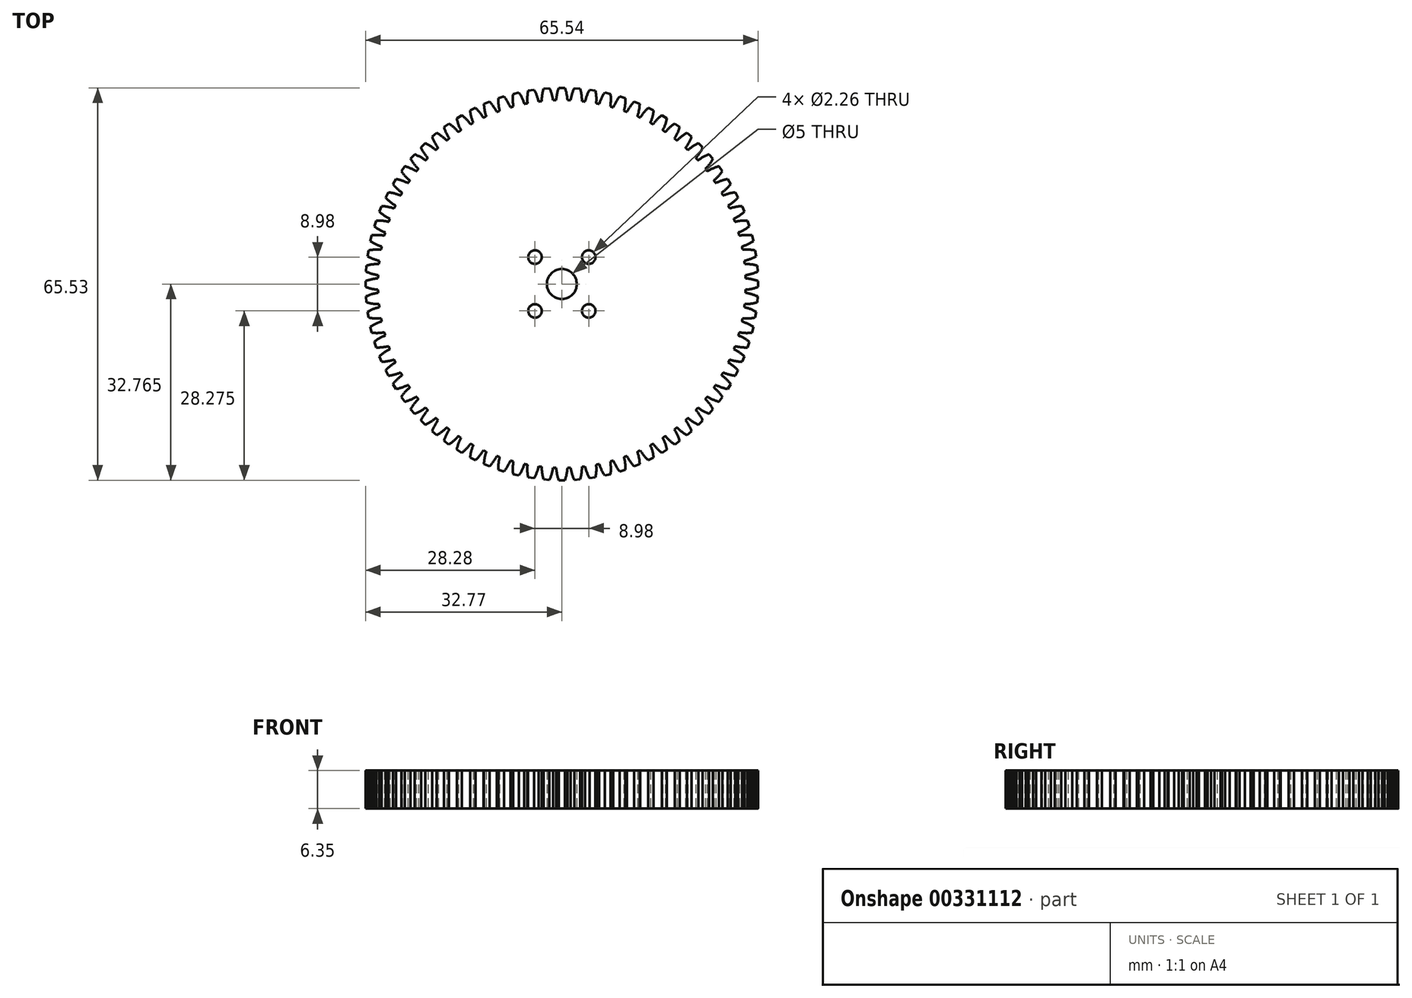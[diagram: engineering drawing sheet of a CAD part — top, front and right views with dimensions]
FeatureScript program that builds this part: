
annotation { "Feature Type Name" : "Feature", "Feature Type Description" : "" }
export const myFeature = defineFeature(function(context is Context, id is Id, definition is map)
    precondition{}
    {
        {
            var Q0;
            Q0=qCreatedBy(makeId("Top.planeOp"),FACE);
            var sketch = newSketch(context, id + "F0", { "sketchPlane" : qUnion([Q0])});
            skLineSegment(sketch, "E0", {"start": v(-0.5, 21.15) * mm, "end": v(0.5, 21.15) * mm});
            skArc(sketch, "E1", {"start": v(-0.5, 21.15) * mm, "mid": v(-0.8, 20.14) * mm, "end": v(-0.94, 19.09) * mm});
            skArc(sketch, "E2.MirrorCS", {"start": v(0.5, 21.15) * mm, "mid": v(0.8, 20.14) * mm, "end": v(0.94, 19.09) * mm});
            skPoint(sketch, "E3.center", {"position": v(0, -11.62) * mm});
            skPoint(sketch, "E4.center", {"position": v(0, 0) * mm});
            skCircle(sketch, "E5.1.1", {"center": v(-4.5, -7.13) * mm, "radius": 1.13 * mm});
            skCircle(sketch, "E5.3.1", {"center": v(-4.5, -16.1) * mm, "radius": 1.13 * mm});
            skCircle(sketch, "E5.5.1", {"center": v(4.5, -16.1) * mm, "radius": 1.13 * mm});
            skCircle(sketch, "E5.7.1", {"center": v(4.5, -7.13) * mm, "radius": 1.13 * mm});
            skArc(sketch, "E6", {"start": v(3.31, 18.92) * mm, "mid": v(2.13, 19.03) * mm, "end": v(0.94, 19.09) * mm});
            skArc(sketch, "E7.1.0", {"start": v(-2.07, 21.09) * mm, "mid": v(-1.7, 20.1) * mm, "end": v(-1.48, 19.07) * mm});
            skLineSegment(sketch, "E7.1.1", {"start": v(-3.07, 21.01) * mm, "end": v(-2.07, 21.09) * mm});
            skArc(sketch, "E7.1.2", {"start": v(-3.07, 21.01) * mm, "mid": v(-3.28, 19.97) * mm, "end": v(-3.34, 18.92) * mm});
            skArc(sketch, "E7.1.3", {"start": v(0.9, 19.09) * mm, "mid": v(-0.28, 19.1) * mm, "end": v(-1.48, 19.07) * mm});
            skArc(sketch, "E7.2.0", {"start": v(-4.63, 20.83) * mm, "mid": v(-4.18, 19.87) * mm, "end": v(-3.88, 18.86) * mm});
            skLineSegment(sketch, "E7.2.1", {"start": v(-5.62, 20.67) * mm, "end": v(-4.63, 20.83) * mm});
            skArc(sketch, "E7.2.2", {"start": v(-5.62, 20.67) * mm, "mid": v(-5.75, 19.62) * mm, "end": v(-5.73, 18.56) * mm});
            skArc(sketch, "E7.2.3", {"start": v(-1.5, 19.06) * mm, "mid": v(-2.7, 18.98) * mm, "end": v(-3.88, 18.86) * mm});
            skArc(sketch, "E7.3.0", {"start": v(-7.16, 20.36) * mm, "mid": v(-6.64, 19.44) * mm, "end": v(-6.26, 18.46) * mm});
            skLineSegment(sketch, "E7.3.1", {"start": v(-8.14, 20.13) * mm, "end": v(-7.16, 20.36) * mm});
            skArc(sketch, "E7.3.2", {"start": v(-8.14, 20.13) * mm, "mid": v(-8.18, 19.07) * mm, "end": v(-8.08, 18.02) * mm});
            skArc(sketch, "E7.3.3", {"start": v(-3.9, 18.85) * mm, "mid": v(-5.09, 18.68) * mm, "end": v(-6.26, 18.46) * mm});
            skArc(sketch, "E7.4.0", {"start": v(-9.65, 19.7) * mm, "mid": v(-9.06, 18.83) * mm, "end": v(-8.6, 17.87) * mm});
            skLineSegment(sketch, "E7.4.1", {"start": v(-10.6, 19.4) * mm, "end": v(-9.65, 19.7) * mm});
            skArc(sketch, "E7.4.2", {"start": v(-10.6, 19.4) * mm, "mid": v(-10.57, 18.34) * mm, "end": v(-10.38, 17.3) * mm});
            skArc(sketch, "E7.4.3", {"start": v(-6.29, 18.45) * mm, "mid": v(-7.45, 18.18) * mm, "end": v(-8.6, 17.87) * mm});
            skArc(sketch, "E7.5.0", {"start": v(-12.08, 18.85) * mm, "mid": v(-11.42, 18.02) * mm, "end": v(-10.88, 17.1) * mm});
            skLineSegment(sketch, "E7.5.1", {"start": v(-13, 18.47) * mm, "end": v(-12.08, 18.85) * mm});
            skArc(sketch, "E7.5.2", {"start": v(-13, 18.47) * mm, "mid": v(-12.88, 17.41) * mm, "end": v(-12.61, 16.4) * mm});
            skArc(sketch, "E7.5.3", {"start": v(-8.63, 17.87) * mm, "mid": v(-9.76, 17.5) * mm, "end": v(-10.88, 17.1) * mm});
            skArc(sketch, "E7.6.0", {"start": v(-14.43, 17.8) * mm, "mid": v(-13.7, 17.04) * mm, "end": v(-13.1, 16.17) * mm});
            skLineSegment(sketch, "E7.6.1", {"start": v(-15.32, 17.35) * mm, "end": v(-14.43, 17.8) * mm});
            skArc(sketch, "E7.6.2", {"start": v(-15.32, 17.35) * mm, "mid": v(-15.12, 16.31) * mm, "end": v(-14.77, 15.32) * mm});
            skArc(sketch, "E7.6.3", {"start": v(-10.91, 17.1) * mm, "mid": v(-12.02, 16.65) * mm, "end": v(-13.1, 16.17) * mm});
            skArc(sketch, "E7.7.0", {"start": v(-16.7, 16.58) * mm, "mid": v(-15.91, 15.87) * mm, "end": v(-15.24, 15.05) * mm});
            skLineSegment(sketch, "E7.7.1", {"start": v(-17.55, 16.06) * mm, "end": v(-16.7, 16.58) * mm});
            skArc(sketch, "E7.7.2", {"start": v(-17.55, 16.06) * mm, "mid": v(-17.27, 15.04) * mm, "end": v(-16.84, 14.07) * mm});
            skArc(sketch, "E7.7.3", {"start": v(-13.13, 16.15) * mm, "mid": v(-14.2, 15.62) * mm, "end": v(-15.24, 15.05) * mm});
            skArc(sketch, "E7.8.0", {"start": v(-18.85, 15.19) * mm, "mid": v(-18.02, 14.54) * mm, "end": v(-17.29, 13.77) * mm});
            skLineSegment(sketch, "E7.8.1", {"start": v(-19.66, 14.6) * mm, "end": v(-18.85, 15.19) * mm});
            skArc(sketch, "E7.8.2", {"start": v(-19.66, 14.6) * mm, "mid": v(-19.3, 13.6) * mm, "end": v(-18.8, 12.67) * mm});
            skArc(sketch, "E7.8.3", {"start": v(-15.27, 15.04) * mm, "mid": v(-16.3, 14.43) * mm, "end": v(-17.29, 13.77) * mm});
            skArc(sketch, "E7.9.0", {"start": v(-20.9, 13.63) * mm, "mid": v(-20.02, 13.04) * mm, "end": v(-19.23, 12.34) * mm});
            skLineSegment(sketch, "E7.9.1", {"start": v(-21.66, 12.98) * mm, "end": v(-20.9, 13.63) * mm});
            skArc(sketch, "E7.9.2", {"start": v(-21.66, 12.98) * mm, "mid": v(-21.22, 12.01) * mm, "end": v(-20.65, 11.12) * mm});
            skArc(sketch, "E7.9.3", {"start": v(-17.31, 13.76) * mm, "mid": v(-18.28, 13.07) * mm, "end": v(-19.23, 12.34) * mm});
            skArc(sketch, "E7.10.0", {"start": v(-22.82, 11.9) * mm, "mid": v(-21.89, 11.4) * mm, "end": v(-21.05, 10.76) * mm});
            skLineSegment(sketch, "E7.10.1", {"start": v(-23.52, 11.2) * mm, "end": v(-22.82, 11.9) * mm});
            skArc(sketch, "E7.10.2", {"start": v(-23.52, 11.2) * mm, "mid": v(-23.01, 10.27) * mm, "end": v(-22.37, 9.43) * mm});
            skArc(sketch, "E7.10.3", {"start": v(-19.25, 12.32) * mm, "mid": v(-20.16, 11.56) * mm, "end": v(-21.05, 10.76) * mm});
            skArc(sketch, "E7.11.0", {"start": v(-24.6, 10.04) * mm, "mid": v(-23.63, 9.6) * mm, "end": v(-22.74, 9.04) * mm});
            skLineSegment(sketch, "E7.11.1", {"start": v(-25.24, 9.28) * mm, "end": v(-24.6, 10.04) * mm});
            skArc(sketch, "E7.11.2", {"start": v(-25.24, 9.28) * mm, "mid": v(-24.66, 8.4) * mm, "end": v(-23.95, 7.61) * mm});
            skArc(sketch, "E7.11.3", {"start": v(-21.07, 10.74) * mm, "mid": v(-21.92, 9.9) * mm, "end": v(-22.74, 9.04) * mm});
            skArc(sketch, "E7.12.0", {"start": v(-26.21, 8.05) * mm, "mid": v(-25.22, 7.7) * mm, "end": v(-24.29, 7.19) * mm});
            skLineSegment(sketch, "E7.12.1", {"start": v(-26.8, 7.24) * mm, "end": v(-26.21, 8.05) * mm});
            skArc(sketch, "E7.12.2", {"start": v(-26.8, 7.24) * mm, "mid": v(-26.15, 6.4) * mm, "end": v(-25.39, 5.67) * mm});
            skArc(sketch, "E7.12.3", {"start": v(-22.76, 9.01) * mm, "mid": v(-23.54, 8.12) * mm, "end": v(-24.29, 7.19) * mm});
            skArc(sketch, "E7.13.0", {"start": v(-27.68, 5.93) * mm, "mid": v(-26.66, 5.65) * mm, "end": v(-25.69, 5.23) * mm});
            skLineSegment(sketch, "E7.13.1", {"start": v(-28.2, 5.08) * mm, "end": v(-27.68, 5.93) * mm});
            skArc(sketch, "E7.13.2", {"start": v(-28.2, 5.08) * mm, "mid": v(-27.49, 4.3) * mm, "end": v(-26.67, 3.63) * mm});
            skArc(sketch, "E7.13.3", {"start": v(-24.3, 7.16) * mm, "mid": v(-25.02, 6.2) * mm, "end": v(-25.69, 5.23) * mm});
            skArc(sketch, "E7.14.0", {"start": v(-28.97, 3.7) * mm, "mid": v(-27.93, 3.5) * mm, "end": v(-26.93, 3.16) * mm});
            skLineSegment(sketch, "E7.14.1", {"start": v(-29.42, 2.81) * mm, "end": v(-28.97, 3.7) * mm});
            skArc(sketch, "E7.14.2", {"start": v(-29.42, 2.81) * mm, "mid": v(-28.65, 2.1) * mm, "end": v(-27.78, 1.49) * mm});
            skArc(sketch, "E7.14.3", {"start": v(-25.7, 5.2) * mm, "mid": v(-26.34, 4.2) * mm, "end": v(-26.93, 3.16) * mm});
            skArc(sketch, "E7.15.0", {"start": v(-30.08, 1.39) * mm, "mid": v(-29.03, 1.27) * mm, "end": v(-28, 1) * mm});
            skLineSegment(sketch, "E7.15.1", {"start": v(-30.46, 0.46) * mm, "end": v(-30.08, 1.39) * mm});
            skArc(sketch, "E7.15.2", {"start": v(-30.46, 0.46) * mm, "mid": v(-29.64, -0.2) * mm, "end": v(-28.72, -0.73) * mm});
            skArc(sketch, "E7.15.3", {"start": v(-26.95, 3.13) * mm, "mid": v(-27.5, 2.08) * mm, "end": v(-28, 1) * mm});
            skArc(sketch, "E7.16.0", {"start": v(-31, -1.01) * mm, "mid": v(-29.95, -1.05) * mm, "end": v(-28.91, -1.24) * mm});
            skLineSegment(sketch, "E7.16.1", {"start": v(-31.32, -1.97) * mm, "end": v(-31, -1.01) * mm});
            skArc(sketch, "E7.16.2", {"start": v(-31.32, -1.97) * mm, "mid": v(-30.44, -2.56) * mm, "end": v(-29.49, -3.02) * mm});
            skArc(sketch, "E7.16.3", {"start": v(-28.02, 0.97) * mm, "mid": v(-28.49, -0.12) * mm, "end": v(-28.91, -1.24) * mm});
            skArc(sketch, "E7.17.0", {"start": v(-31.74, -3.48) * mm, "mid": v(-30.69, -3.43) * mm, "end": v(-29.64, -3.54) * mm});
            skLineSegment(sketch, "E7.17.1", {"start": v(-31.98, -4.45) * mm, "end": v(-31.74, -3.48) * mm});
            skArc(sketch, "E7.17.2", {"start": v(-31.98, -4.45) * mm, "mid": v(-31.06, -4.98) * mm, "end": v(-30.07, -5.36) * mm});
            skArc(sketch, "E7.17.3", {"start": v(-28.92, -1.27) * mm, "mid": v(-29.3, -2.4) * mm, "end": v(-29.64, -3.54) * mm});
            skArc(sketch, "E7.18.0", {"start": v(-32.28, -6) * mm, "mid": v(-31.24, -5.86) * mm, "end": v(-30.18, -5.89) * mm});
            skLineSegment(sketch, "E7.18.1", {"start": v(-32.44, -6.98) * mm, "end": v(-32.28, -6) * mm});
            skArc(sketch, "E7.18.2", {"start": v(-32.44, -6.98) * mm, "mid": v(-31.48, -7.43) * mm, "end": v(-30.47, -7.74) * mm});
            skArc(sketch, "E7.18.3", {"start": v(-29.64, -3.57) * mm, "mid": v(-29.93, -4.72) * mm, "end": v(-30.18, -5.89) * mm});
            skArc(sketch, "E7.19.0", {"start": v(-32.63, -8.55) * mm, "mid": v(-31.6, -8.33) * mm, "end": v(-30.53, -8.27) * mm});
            skLineSegment(sketch, "E7.19.1", {"start": v(-32.7, -9.54) * mm, "end": v(-32.63, -8.55) * mm});
            skArc(sketch, "E7.19.2", {"start": v(-32.7, -9.54) * mm, "mid": v(-31.71, -9.92) * mm, "end": v(-30.68, -10.14) * mm});
            skArc(sketch, "E7.19.3", {"start": v(-30.18, -5.92) * mm, "mid": v(-30.38, -7.1) * mm, "end": v(-30.53, -8.27) * mm});
            skArc(sketch, "E7.20.0", {"start": v(-32.77, -11.12) * mm, "mid": v(-31.75, -10.82) * mm, "end": v(-30.7, -10.68) * mm});
            skLineSegment(sketch, "E7.20.1", {"start": v(-32.77, -12.12) * mm, "end": v(-32.77, -11.12) * mm});
            skArc(sketch, "E7.20.2", {"start": v(-32.77, -12.12) * mm, "mid": v(-31.75, -12.4) * mm, "end": v(-30.7, -12.55) * mm});
            skArc(sketch, "E7.20.3", {"start": v(-30.54, -8.3) * mm, "mid": v(-30.64, -9.49) * mm, "end": v(-30.7, -10.68) * mm});
            skArc(sketch, "E7.21.0", {"start": v(-32.7, -13.69) * mm, "mid": v(-31.71, -13.31) * mm, "end": v(-30.68, -13.1) * mm});
            skLineSegment(sketch, "E7.21.1", {"start": v(-32.63, -14.68) * mm, "end": v(-32.7, -13.69) * mm});
            skArc(sketch, "E7.21.2", {"start": v(-32.63, -14.68) * mm, "mid": v(-31.6, -14.9) * mm, "end": v(-30.53, -14.96) * mm});
            skArc(sketch, "E7.21.3", {"start": v(-30.7, -10.7) * mm, "mid": v(-30.72, -11.9) * mm, "end": v(-30.68, -13.1) * mm});
            skArc(sketch, "E7.22.0", {"start": v(-32.44, -16.25) * mm, "mid": v(-31.48, -15.8) * mm, "end": v(-30.47, -15.5) * mm});
            skLineSegment(sketch, "E7.22.1", {"start": v(-32.28, -17.23) * mm, "end": v(-32.44, -16.25) * mm});
            skArc(sketch, "E7.22.2", {"start": v(-32.28, -17.23) * mm, "mid": v(-31.24, -17.37) * mm, "end": v(-30.18, -17.34) * mm});
            skArc(sketch, "E7.22.3", {"start": v(-30.68, -13.12) * mm, "mid": v(-30.6, -14.3) * mm, "end": v(-30.47, -15.5) * mm});
            skArc(sketch, "E7.23.0", {"start": v(-31.98, -18.78) * mm, "mid": v(-31.06, -18.25) * mm, "end": v(-30.07, -17.87) * mm});
            skLineSegment(sketch, "E7.23.1", {"start": v(-31.74, -19.75) * mm, "end": v(-31.98, -18.78) * mm});
            skArc(sketch, "E7.23.2", {"start": v(-31.74, -19.75) * mm, "mid": v(-30.69, -19.8) * mm, "end": v(-29.64, -19.7) * mm});
            skArc(sketch, "E7.23.3", {"start": v(-30.47, -15.52) * mm, "mid": v(-30.3, -16.7) * mm, "end": v(-30.07, -17.87) * mm});
            skArc(sketch, "E7.24.0", {"start": v(-31.32, -21.26) * mm, "mid": v(-30.44, -20.67) * mm, "end": v(-29.49, -20.21) * mm});
            skLineSegment(sketch, "E7.24.1", {"start": v(-31, -22.22) * mm, "end": v(-31.32, -21.26) * mm});
            skArc(sketch, "E7.24.2", {"start": v(-31, -22.22) * mm, "mid": v(-29.95, -22.18) * mm, "end": v(-28.91, -22) * mm});
            skArc(sketch, "E7.24.3", {"start": v(-30.07, -17.9) * mm, "mid": v(-29.8, -19.06) * mm, "end": v(-29.49, -20.21) * mm});
            skArc(sketch, "E7.25.0", {"start": v(-30.46, -23.7) * mm, "mid": v(-29.64, -23.03) * mm, "end": v(-28.72, -22.5) * mm});
            skLineSegment(sketch, "E7.25.1", {"start": v(-30.08, -24.62) * mm, "end": v(-30.46, -23.7) * mm});
            skArc(sketch, "E7.25.2", {"start": v(-30.08, -24.62) * mm, "mid": v(-29.03, -24.5) * mm, "end": v(-28, -24.23) * mm});
            skArc(sketch, "E7.25.3", {"start": v(-29.48, -20.24) * mm, "mid": v(-29.12, -21.38) * mm, "end": v(-28.72, -22.5) * mm});
            skArc(sketch, "E7.26.0", {"start": v(-29.42, -26.05) * mm, "mid": v(-28.65, -25.32) * mm, "end": v(-27.78, -24.72) * mm});
            skLineSegment(sketch, "E7.26.1", {"start": v(-28.97, -26.94) * mm, "end": v(-29.42, -26.05) * mm});
            skArc(sketch, "E7.26.2", {"start": v(-28.97, -26.94) * mm, "mid": v(-27.93, -26.74) * mm, "end": v(-26.93, -26.39) * mm});
            skArc(sketch, "E7.26.3", {"start": v(-28.71, -22.53) * mm, "mid": v(-28.27, -23.63) * mm, "end": v(-27.78, -24.72) * mm});
            skArc(sketch, "E7.27.0", {"start": v(-28.2, -28.3) * mm, "mid": v(-27.49, -27.53) * mm, "end": v(-26.67, -26.86) * mm});
            skLineSegment(sketch, "E7.27.1", {"start": v(-27.68, -29.16) * mm, "end": v(-28.2, -28.3) * mm});
            skArc(sketch, "E7.27.2", {"start": v(-27.68, -29.16) * mm, "mid": v(-26.66, -28.88) * mm, "end": v(-25.69, -28.46) * mm});
            skArc(sketch, "E7.27.3", {"start": v(-27.77, -24.75) * mm, "mid": v(-27.24, -25.81) * mm, "end": v(-26.67, -26.86) * mm});
            skArc(sketch, "E7.28.0", {"start": v(-26.8, -30.47) * mm, "mid": v(-26.15, -29.63) * mm, "end": v(-25.39, -28.9) * mm});
            skLineSegment(sketch, "E7.28.1", {"start": v(-26.21, -31.28) * mm, "end": v(-26.8, -30.47) * mm});
            skArc(sketch, "E7.28.2", {"start": v(-26.21, -31.28) * mm, "mid": v(-25.22, -30.92) * mm, "end": v(-24.29, -30.42) * mm});
            skArc(sketch, "E7.28.3", {"start": v(-26.65, -26.88) * mm, "mid": v(-26.04, -27.9) * mm, "end": v(-25.39, -28.9) * mm});
            skArc(sketch, "E7.29.0", {"start": v(-25.24, -32.51) * mm, "mid": v(-24.66, -31.63) * mm, "end": v(-23.95, -30.84) * mm});
            skLineSegment(sketch, "E7.29.1", {"start": v(-24.6, -33.28) * mm, "end": v(-25.24, -32.51) * mm});
            skArc(sketch, "E7.29.2", {"start": v(-24.6, -33.28) * mm, "mid": v(-23.63, -32.84) * mm, "end": v(-22.74, -32.27) * mm});
            skArc(sketch, "E7.29.3", {"start": v(-25.37, -28.93) * mm, "mid": v(-24.68, -29.9) * mm, "end": v(-23.95, -30.84) * mm});
            skArc(sketch, "E7.30.0", {"start": v(-23.52, -34.43) * mm, "mid": v(-23.01, -33.5) * mm, "end": v(-22.37, -32.66) * mm});
            skLineSegment(sketch, "E7.30.1", {"start": v(-22.82, -35.14) * mm, "end": v(-23.52, -34.43) * mm});
            skArc(sketch, "E7.30.2", {"start": v(-22.82, -35.14) * mm, "mid": v(-21.89, -34.63) * mm, "end": v(-21.05, -33.99) * mm});
            skArc(sketch, "E7.30.3", {"start": v(-23.94, -30.87) * mm, "mid": v(-23.17, -31.78) * mm, "end": v(-22.37, -32.66) * mm});
            skArc(sketch, "E7.31.0", {"start": v(-21.66, -36.2) * mm, "mid": v(-21.22, -35.24) * mm, "end": v(-20.65, -34.35) * mm});
            skLineSegment(sketch, "E7.31.1", {"start": v(-20.9, -36.86) * mm, "end": v(-21.66, -36.2) * mm});
            skArc(sketch, "E7.31.2", {"start": v(-20.9, -36.86) * mm, "mid": v(-20.02, -36.27) * mm, "end": v(-19.23, -35.57) * mm});
            skArc(sketch, "E7.31.3", {"start": v(-22.35, -32.68) * mm, "mid": v(-21.52, -33.54) * mm, "end": v(-20.65, -34.35) * mm});
            skArc(sketch, "E7.32.0", {"start": v(-19.66, -37.83) * mm, "mid": v(-19.3, -36.83) * mm, "end": v(-18.8, -35.9) * mm});
            skLineSegment(sketch, "E7.32.1", {"start": v(-18.85, -38.42) * mm, "end": v(-19.66, -37.83) * mm});
            skArc(sketch, "E7.32.2", {"start": v(-18.85, -38.42) * mm, "mid": v(-18.02, -37.77) * mm, "end": v(-17.29, -37) * mm});
            skArc(sketch, "E7.32.3", {"start": v(-20.63, -34.37) * mm, "mid": v(-19.73, -35.16) * mm, "end": v(-18.8, -35.9) * mm});
            skArc(sketch, "E7.33.0", {"start": v(-17.55, -39.3) * mm, "mid": v(-17.27, -38.27) * mm, "end": v(-16.84, -37.3) * mm});
            skLineSegment(sketch, "E7.33.1", {"start": v(-16.7, -39.81) * mm, "end": v(-17.55, -39.3) * mm});
            skArc(sketch, "E7.33.2", {"start": v(-16.7, -39.81) * mm, "mid": v(-15.91, -39.1) * mm, "end": v(-15.24, -38.28) * mm});
            skArc(sketch, "E7.33.3", {"start": v(-18.78, -35.92) * mm, "mid": v(-17.82, -36.63) * mm, "end": v(-16.84, -37.3) * mm});
            skArc(sketch, "E7.34.0", {"start": v(-15.32, -40.58) * mm, "mid": v(-15.12, -39.54) * mm, "end": v(-14.77, -38.55) * mm});
            skLineSegment(sketch, "E7.34.1", {"start": v(-14.43, -41.04) * mm, "end": v(-15.32, -40.58) * mm});
            skArc(sketch, "E7.34.2", {"start": v(-14.43, -41.04) * mm, "mid": v(-13.7, -40.27) * mm, "end": v(-13.1, -39.4) * mm});
            skArc(sketch, "E7.34.3", {"start": v(-16.81, -37.32) * mm, "mid": v(-15.8, -37.95) * mm, "end": v(-14.77, -38.55) * mm});
            skArc(sketch, "E7.35.0", {"start": v(-13, -41.7) * mm, "mid": v(-12.88, -40.64) * mm, "end": v(-12.61, -39.62) * mm});
            skLineSegment(sketch, "E7.35.1", {"start": v(-12.08, -42.08) * mm, "end": v(-13, -41.7) * mm});
            skArc(sketch, "E7.35.2", {"start": v(-12.08, -42.08) * mm, "mid": v(-11.42, -41.25) * mm, "end": v(-10.88, -40.34) * mm});
            skArc(sketch, "E7.35.3", {"start": v(-14.75, -38.56) * mm, "mid": v(-13.7, -39.11) * mm, "end": v(-12.61, -39.62) * mm});
            skArc(sketch, "E7.36.0", {"start": v(-10.6, -42.62) * mm, "mid": v(-10.57, -41.57) * mm, "end": v(-10.38, -40.53) * mm});
            skLineSegment(sketch, "E7.36.1", {"start": v(-9.65, -42.93) * mm, "end": v(-10.6, -42.62) * mm});
            skArc(sketch, "E7.36.2", {"start": v(-9.65, -42.93) * mm, "mid": v(-9.06, -42.06) * mm, "end": v(-8.6, -41.1) * mm});
            skArc(sketch, "E7.36.3", {"start": v(-12.59, -39.63) * mm, "mid": v(-11.5, -40.1) * mm, "end": v(-10.38, -40.53) * mm});
            skArc(sketch, "E7.37.0", {"start": v(-8.14, -43.36) * mm, "mid": v(-8.18, -42.3) * mm, "end": v(-8.08, -41.25) * mm});
            skLineSegment(sketch, "E7.37.1", {"start": v(-7.16, -43.6) * mm, "end": v(-8.14, -43.36) * mm});
            skArc(sketch, "E7.37.2", {"start": v(-7.16, -43.6) * mm, "mid": v(-6.64, -42.67) * mm, "end": v(-6.26, -41.69) * mm});
            skArc(sketch, "E7.37.3", {"start": v(-10.35, -40.54) * mm, "mid": v(-9.22, -40.92) * mm, "end": v(-8.08, -41.25) * mm});
            skArc(sketch, "E7.38.0", {"start": v(-5.62, -43.9) * mm, "mid": v(-5.75, -42.85) * mm, "end": v(-5.73, -41.8) * mm});
            skLineSegment(sketch, "E7.38.1", {"start": v(-4.63, -44.06) * mm, "end": v(-5.62, -43.9) * mm});
            skArc(sketch, "E7.38.2", {"start": v(-4.63, -44.06) * mm, "mid": v(-4.18, -43.1) * mm, "end": v(-3.88, -42.09) * mm});
            skArc(sketch, "E7.38.3", {"start": v(-8.05, -41.26) * mm, "mid": v(-6.9, -41.55) * mm, "end": v(-5.73, -41.8) * mm});
            skArc(sketch, "E7.39.0", {"start": v(-3.07, -44.24) * mm, "mid": v(-3.28, -43.2) * mm, "end": v(-3.34, -42.15) * mm});
            skLineSegment(sketch, "E7.39.1", {"start": v(-2.07, -44.32) * mm, "end": v(-3.07, -44.24) * mm});
            skArc(sketch, "E7.39.2", {"start": v(-2.07, -44.32) * mm, "mid": v(-1.7, -43.33) * mm, "end": v(-1.48, -42.3) * mm});
            skArc(sketch, "E7.39.3", {"start": v(-5.7, -41.8) * mm, "mid": v(-4.52, -42) * mm, "end": v(-3.34, -42.15) * mm});
            skCircle(sketch, "E8", {"center": v(0, -11.62) * mm, "radius": 2.5 * mm});
            skLineSegment(sketch, "E9.4.40.0", {"start": v(0.5, -44.38) * mm, "end": v(-0.5, -44.38) * mm});
            skArc(sketch, "E9.7.40.0", {"start": v(0.5, -44.38) * mm, "mid": v(0.8, -43.37) * mm, "end": v(0.94, -42.32) * mm});
            skArc(sketch, "E9.11.40.0", {"start": v(-3.31, -42.15) * mm, "mid": v(-2.13, -42.26) * mm, "end": v(-0.94, -42.32) * mm});
            skArc(sketch, "E9.12.40.0", {"start": v(-0.5, -44.38) * mm, "mid": v(-0.8, -43.37) * mm, "end": v(-0.94, -42.32) * mm});
            skLineSegment(sketch, "E9.4.41.0", {"start": v(3.07, -44.24) * mm, "end": v(2.07, -44.32) * mm});
            skArc(sketch, "E9.7.41.0", {"start": v(3.07, -44.24) * mm, "mid": v(3.28, -43.2) * mm, "end": v(3.34, -42.15) * mm});
            skArc(sketch, "E9.11.41.0", {"start": v(-0.9, -42.32) * mm, "mid": v(0.28, -42.33) * mm, "end": v(1.48, -42.3) * mm});
            skArc(sketch, "E9.12.41.0", {"start": v(2.07, -44.32) * mm, "mid": v(1.7, -43.33) * mm, "end": v(1.48, -42.3) * mm});
            skLineSegment(sketch, "E9.4.42.0", {"start": v(5.62, -43.9) * mm, "end": v(4.63, -44.06) * mm});
            skArc(sketch, "E9.7.42.0", {"start": v(5.62, -43.9) * mm, "mid": v(5.75, -42.85) * mm, "end": v(5.73, -41.8) * mm});
            skArc(sketch, "E9.11.42.0", {"start": v(1.5, -42.3) * mm, "mid": v(2.7, -42.21) * mm, "end": v(3.88, -42.09) * mm});
            skArc(sketch, "E9.12.42.0", {"start": v(4.63, -44.06) * mm, "mid": v(4.18, -43.1) * mm, "end": v(3.88, -42.09) * mm});
            skLineSegment(sketch, "E9.4.43.0", {"start": v(8.14, -43.36) * mm, "end": v(7.16, -43.6) * mm});
            skArc(sketch, "E9.7.43.0", {"start": v(8.14, -43.36) * mm, "mid": v(8.18, -42.3) * mm, "end": v(8.08, -41.25) * mm});
            skArc(sketch, "E9.11.43.0", {"start": v(3.9, -42.08) * mm, "mid": v(5.09, -41.9) * mm, "end": v(6.26, -41.69) * mm});
            skArc(sketch, "E9.12.43.0", {"start": v(7.16, -43.6) * mm, "mid": v(6.64, -42.67) * mm, "end": v(6.26, -41.69) * mm});
            skLineSegment(sketch, "E9.4.44.0", {"start": v(10.6, -42.62) * mm, "end": v(9.65, -42.93) * mm});
            skArc(sketch, "E9.7.44.0", {"start": v(10.6, -42.62) * mm, "mid": v(10.57, -41.57) * mm, "end": v(10.38, -40.53) * mm});
            skArc(sketch, "E9.11.44.0", {"start": v(6.29, -41.68) * mm, "mid": v(7.45, -41.42) * mm, "end": v(8.6, -41.1) * mm});
            skArc(sketch, "E9.12.44.0", {"start": v(9.65, -42.93) * mm, "mid": v(9.06, -42.06) * mm, "end": v(8.6, -41.1) * mm});
            skLineSegment(sketch, "E9.4.45.0", {"start": v(13, -41.7) * mm, "end": v(12.08, -42.08) * mm});
            skArc(sketch, "E9.7.45.0", {"start": v(13, -41.7) * mm, "mid": v(12.88, -40.64) * mm, "end": v(12.61, -39.62) * mm});
            skArc(sketch, "E9.11.45.0", {"start": v(8.63, -41.1) * mm, "mid": v(9.76, -40.74) * mm, "end": v(10.88, -40.34) * mm});
            skArc(sketch, "E9.12.45.0", {"start": v(12.08, -42.08) * mm, "mid": v(11.42, -41.25) * mm, "end": v(10.88, -40.34) * mm});
            skLineSegment(sketch, "E9.4.46.0", {"start": v(15.32, -40.58) * mm, "end": v(14.43, -41.04) * mm});
            skArc(sketch, "E9.7.46.0", {"start": v(15.32, -40.58) * mm, "mid": v(15.12, -39.54) * mm, "end": v(14.77, -38.55) * mm});
            skArc(sketch, "E9.11.46.0", {"start": v(10.91, -40.33) * mm, "mid": v(12.02, -39.88) * mm, "end": v(13.1, -39.4) * mm});
            skArc(sketch, "E9.12.46.0", {"start": v(14.43, -41.04) * mm, "mid": v(13.7, -40.27) * mm, "end": v(13.1, -39.4) * mm});
            skLineSegment(sketch, "E9.4.47.0", {"start": v(17.55, -39.3) * mm, "end": v(16.7, -39.81) * mm});
            skArc(sketch, "E9.7.47.0", {"start": v(17.55, -39.3) * mm, "mid": v(17.27, -38.27) * mm, "end": v(16.84, -37.3) * mm});
            skArc(sketch, "E9.11.47.0", {"start": v(13.13, -39.38) * mm, "mid": v(14.2, -38.85) * mm, "end": v(15.24, -38.28) * mm});
            skArc(sketch, "E9.12.47.0", {"start": v(16.7, -39.81) * mm, "mid": v(15.91, -39.1) * mm, "end": v(15.24, -38.28) * mm});
            skLineSegment(sketch, "E9.4.48.0", {"start": v(19.66, -37.83) * mm, "end": v(18.85, -38.42) * mm});
            skArc(sketch, "E9.7.48.0", {"start": v(19.66, -37.83) * mm, "mid": v(19.3, -36.83) * mm, "end": v(18.8, -35.9) * mm});
            skArc(sketch, "E9.11.48.0", {"start": v(15.27, -38.27) * mm, "mid": v(16.3, -37.66) * mm, "end": v(17.29, -37) * mm});
            skArc(sketch, "E9.12.48.0", {"start": v(18.85, -38.42) * mm, "mid": v(18.02, -37.77) * mm, "end": v(17.29, -37) * mm});
            skLineSegment(sketch, "E9.4.49.0", {"start": v(21.66, -36.2) * mm, "end": v(20.9, -36.86) * mm});
            skArc(sketch, "E9.7.49.0", {"start": v(21.66, -36.2) * mm, "mid": v(21.22, -35.24) * mm, "end": v(20.65, -34.35) * mm});
            skArc(sketch, "E9.11.49.0", {"start": v(17.31, -36.99) * mm, "mid": v(18.28, -36.3) * mm, "end": v(19.23, -35.57) * mm});
            skArc(sketch, "E9.12.49.0", {"start": v(20.9, -36.86) * mm, "mid": v(20.02, -36.27) * mm, "end": v(19.23, -35.57) * mm});
            skLineSegment(sketch, "E9.4.50.0", {"start": v(23.52, -34.43) * mm, "end": v(22.82, -35.14) * mm});
            skArc(sketch, "E9.7.50.0", {"start": v(23.52, -34.43) * mm, "mid": v(23.01, -33.5) * mm, "end": v(22.37, -32.66) * mm});
            skArc(sketch, "E9.11.50.0", {"start": v(19.25, -35.55) * mm, "mid": v(20.16, -34.79) * mm, "end": v(21.05, -33.99) * mm});
            skArc(sketch, "E9.12.50.0", {"start": v(22.82, -35.14) * mm, "mid": v(21.89, -34.63) * mm, "end": v(21.05, -33.99) * mm});
            skLineSegment(sketch, "E9.4.51.0", {"start": v(25.24, -32.51) * mm, "end": v(24.6, -33.28) * mm});
            skArc(sketch, "E9.7.51.0", {"start": v(25.24, -32.51) * mm, "mid": v(24.66, -31.63) * mm, "end": v(23.95, -30.84) * mm});
            skArc(sketch, "E9.11.51.0", {"start": v(21.07, -33.97) * mm, "mid": v(21.92, -33.13) * mm, "end": v(22.74, -32.27) * mm});
            skArc(sketch, "E9.12.51.0", {"start": v(24.6, -33.28) * mm, "mid": v(23.63, -32.84) * mm, "end": v(22.74, -32.27) * mm});
            skLineSegment(sketch, "E9.4.52.0", {"start": v(26.8, -30.47) * mm, "end": v(26.21, -31.28) * mm});
            skArc(sketch, "E9.7.52.0", {"start": v(26.8, -30.47) * mm, "mid": v(26.15, -29.63) * mm, "end": v(25.39, -28.9) * mm});
            skArc(sketch, "E9.11.52.0", {"start": v(22.76, -32.24) * mm, "mid": v(23.54, -31.35) * mm, "end": v(24.29, -30.42) * mm});
            skArc(sketch, "E9.12.52.0", {"start": v(26.21, -31.28) * mm, "mid": v(25.22, -30.92) * mm, "end": v(24.29, -30.42) * mm});
            skLineSegment(sketch, "E9.4.53.0", {"start": v(28.2, -28.3) * mm, "end": v(27.68, -29.16) * mm});
            skArc(sketch, "E9.7.53.0", {"start": v(28.2, -28.3) * mm, "mid": v(27.49, -27.53) * mm, "end": v(26.67, -26.86) * mm});
            skArc(sketch, "E9.11.53.0", {"start": v(24.3, -30.4) * mm, "mid": v(25.02, -29.44) * mm, "end": v(25.69, -28.46) * mm});
            skArc(sketch, "E9.12.53.0", {"start": v(27.68, -29.16) * mm, "mid": v(26.66, -28.88) * mm, "end": v(25.69, -28.46) * mm});
            skLineSegment(sketch, "E9.4.54.0", {"start": v(29.42, -26.05) * mm, "end": v(28.97, -26.94) * mm});
            skArc(sketch, "E9.7.54.0", {"start": v(29.42, -26.05) * mm, "mid": v(28.65, -25.32) * mm, "end": v(27.78, -24.72) * mm});
            skArc(sketch, "E9.11.54.0", {"start": v(25.7, -28.43) * mm, "mid": v(26.34, -27.42) * mm, "end": v(26.93, -26.39) * mm});
            skArc(sketch, "E9.12.54.0", {"start": v(28.97, -26.94) * mm, "mid": v(27.93, -26.74) * mm, "end": v(26.93, -26.39) * mm});
            skLineSegment(sketch, "E9.4.55.0", {"start": v(30.46, -23.7) * mm, "end": v(30.08, -24.62) * mm});
            skArc(sketch, "E9.7.55.0", {"start": v(30.46, -23.7) * mm, "mid": v(29.64, -23.03) * mm, "end": v(28.72, -22.5) * mm});
            skArc(sketch, "E9.11.55.0", {"start": v(26.95, -26.36) * mm, "mid": v(27.5, -25.3) * mm, "end": v(28, -24.23) * mm});
            skArc(sketch, "E9.12.55.0", {"start": v(30.08, -24.62) * mm, "mid": v(29.03, -24.5) * mm, "end": v(28, -24.23) * mm});
            skLineSegment(sketch, "E9.4.56.0", {"start": v(31.32, -21.26) * mm, "end": v(31, -22.22) * mm});
            skArc(sketch, "E9.7.56.0", {"start": v(31.32, -21.26) * mm, "mid": v(30.44, -20.67) * mm, "end": v(29.49, -20.21) * mm});
            skArc(sketch, "E9.11.56.0", {"start": v(28.02, -24.2) * mm, "mid": v(28.49, -23.1) * mm, "end": v(28.91, -22) * mm});
            skArc(sketch, "E9.12.56.0", {"start": v(31, -22.22) * mm, "mid": v(29.95, -22.18) * mm, "end": v(28.91, -22) * mm});
            skLineSegment(sketch, "E9.4.57.0", {"start": v(31.98, -18.78) * mm, "end": v(31.74, -19.75) * mm});
            skArc(sketch, "E9.7.57.0", {"start": v(31.98, -18.78) * mm, "mid": v(31.06, -18.25) * mm, "end": v(30.07, -17.87) * mm});
            skArc(sketch, "E9.11.57.0", {"start": v(28.92, -21.96) * mm, "mid": v(29.3, -20.84) * mm, "end": v(29.64, -19.7) * mm});
            skArc(sketch, "E9.12.57.0", {"start": v(31.74, -19.75) * mm, "mid": v(30.69, -19.8) * mm, "end": v(29.64, -19.7) * mm});
            skLineSegment(sketch, "E9.4.58.0", {"start": v(32.44, -16.25) * mm, "end": v(32.28, -17.23) * mm});
            skArc(sketch, "E9.7.58.0", {"start": v(32.44, -16.25) * mm, "mid": v(31.48, -15.8) * mm, "end": v(30.47, -15.5) * mm});
            skArc(sketch, "E9.11.58.0", {"start": v(29.64, -19.66) * mm, "mid": v(29.93, -18.5) * mm, "end": v(30.18, -17.34) * mm});
            skArc(sketch, "E9.12.58.0", {"start": v(32.28, -17.23) * mm, "mid": v(31.24, -17.37) * mm, "end": v(30.18, -17.34) * mm});
            skLineSegment(sketch, "E9.4.59.0", {"start": v(32.7, -13.69) * mm, "end": v(32.63, -14.68) * mm});
            skArc(sketch, "E9.7.59.0", {"start": v(32.7, -13.69) * mm, "mid": v(31.71, -13.31) * mm, "end": v(30.68, -13.1) * mm});
            skArc(sketch, "E9.11.59.0", {"start": v(30.18, -17.31) * mm, "mid": v(30.38, -16.14) * mm, "end": v(30.53, -14.96) * mm});
            skArc(sketch, "E9.12.59.0", {"start": v(32.63, -14.68) * mm, "mid": v(31.6, -14.9) * mm, "end": v(30.53, -14.96) * mm});
            skLineSegment(sketch, "E9.4.60.0", {"start": v(32.77, -11.12) * mm, "end": v(32.77, -12.12) * mm});
            skArc(sketch, "E9.7.60.0", {"start": v(32.77, -11.12) * mm, "mid": v(31.75, -10.82) * mm, "end": v(30.7, -10.68) * mm});
            skArc(sketch, "E9.11.60.0", {"start": v(30.54, -14.93) * mm, "mid": v(30.64, -13.74) * mm, "end": v(30.7, -12.55) * mm});
            skArc(sketch, "E9.12.60.0", {"start": v(32.77, -12.12) * mm, "mid": v(31.75, -12.4) * mm, "end": v(30.7, -12.55) * mm});
            skLineSegment(sketch, "E9.4.61.0", {"start": v(32.63, -8.55) * mm, "end": v(32.7, -9.54) * mm});
            skArc(sketch, "E9.7.61.0", {"start": v(32.63, -8.55) * mm, "mid": v(31.6, -8.33) * mm, "end": v(30.53, -8.27) * mm});
            skArc(sketch, "E9.11.61.0", {"start": v(30.7, -12.52) * mm, "mid": v(30.72, -11.33) * mm, "end": v(30.68, -10.14) * mm});
            skArc(sketch, "E9.12.61.0", {"start": v(32.7, -9.54) * mm, "mid": v(31.71, -9.92) * mm, "end": v(30.68, -10.14) * mm});
            skLineSegment(sketch, "E9.4.62.0", {"start": v(32.28, -6) * mm, "end": v(32.44, -6.98) * mm});
            skArc(sketch, "E9.7.62.0", {"start": v(32.28, -6) * mm, "mid": v(31.24, -5.86) * mm, "end": v(30.18, -5.89) * mm});
            skArc(sketch, "E9.11.62.0", {"start": v(30.68, -10.1) * mm, "mid": v(30.6, -8.92) * mm, "end": v(30.47, -7.74) * mm});
            skArc(sketch, "E9.12.62.0", {"start": v(32.44, -6.98) * mm, "mid": v(31.48, -7.43) * mm, "end": v(30.47, -7.74) * mm});
            skLineSegment(sketch, "E9.4.63.0", {"start": v(31.74, -3.48) * mm, "end": v(31.98, -4.45) * mm});
            skArc(sketch, "E9.7.63.0", {"start": v(31.74, -3.48) * mm, "mid": v(30.69, -3.43) * mm, "end": v(29.64, -3.54) * mm});
            skArc(sketch, "E9.11.63.0", {"start": v(30.47, -7.7) * mm, "mid": v(30.3, -6.53) * mm, "end": v(30.07, -5.36) * mm});
            skArc(sketch, "E9.12.63.0", {"start": v(31.98, -4.45) * mm, "mid": v(31.06, -4.98) * mm, "end": v(30.07, -5.36) * mm});
            skLineSegment(sketch, "E9.4.64.0", {"start": v(31, -1.01) * mm, "end": v(31.32, -1.97) * mm});
            skArc(sketch, "E9.7.64.0", {"start": v(31, -1.01) * mm, "mid": v(29.95, -1.05) * mm, "end": v(28.91, -1.24) * mm});
            skArc(sketch, "E9.11.64.0", {"start": v(30.07, -5.33) * mm, "mid": v(29.8, -4.17) * mm, "end": v(29.49, -3.02) * mm});
            skArc(sketch, "E9.12.64.0", {"start": v(31.32, -1.97) * mm, "mid": v(30.44, -2.56) * mm, "end": v(29.49, -3.02) * mm});
            skLineSegment(sketch, "E9.4.65.0", {"start": v(30.08, 1.39) * mm, "end": v(30.46, 0.46) * mm});
            skArc(sketch, "E9.7.65.0", {"start": v(30.08, 1.39) * mm, "mid": v(29.03, 1.27) * mm, "end": v(28, 1) * mm});
            skArc(sketch, "E9.11.65.0", {"start": v(29.48, -2.99) * mm, "mid": v(29.12, -1.85) * mm, "end": v(28.72, -0.73) * mm});
            skArc(sketch, "E9.12.65.0", {"start": v(30.46, 0.46) * mm, "mid": v(29.64, -0.2) * mm, "end": v(28.72, -0.73) * mm});
            skLineSegment(sketch, "E9.4.66.0", {"start": v(28.97, 3.7) * mm, "end": v(29.42, 2.81) * mm});
            skArc(sketch, "E9.7.66.0", {"start": v(28.97, 3.7) * mm, "mid": v(27.93, 3.5) * mm, "end": v(26.93, 3.16) * mm});
            skArc(sketch, "E9.11.66.0", {"start": v(28.71, -0.7) * mm, "mid": v(28.27, 0.4) * mm, "end": v(27.78, 1.49) * mm});
            skArc(sketch, "E9.12.66.0", {"start": v(29.42, 2.81) * mm, "mid": v(28.65, 2.1) * mm, "end": v(27.78, 1.49) * mm});
            skLineSegment(sketch, "E9.4.67.0", {"start": v(27.68, 5.93) * mm, "end": v(28.2, 5.08) * mm});
            skArc(sketch, "E9.7.67.0", {"start": v(27.68, 5.93) * mm, "mid": v(26.66, 5.65) * mm, "end": v(25.69, 5.23) * mm});
            skArc(sketch, "E9.11.67.0", {"start": v(27.77, 1.52) * mm, "mid": v(27.24, 2.58) * mm, "end": v(26.67, 3.63) * mm});
            skArc(sketch, "E9.12.67.0", {"start": v(28.2, 5.08) * mm, "mid": v(27.49, 4.3) * mm, "end": v(26.67, 3.63) * mm});
            skLineSegment(sketch, "E9.4.68.0", {"start": v(26.21, 8.05) * mm, "end": v(26.8, 7.24) * mm});
            skArc(sketch, "E9.7.68.0", {"start": v(26.21, 8.05) * mm, "mid": v(25.22, 7.7) * mm, "end": v(24.29, 7.19) * mm});
            skArc(sketch, "E9.11.68.0", {"start": v(26.65, 3.65) * mm, "mid": v(26.04, 4.68) * mm, "end": v(25.39, 5.67) * mm});
            skArc(sketch, "E9.12.68.0", {"start": v(26.8, 7.24) * mm, "mid": v(26.15, 6.4) * mm, "end": v(25.39, 5.67) * mm});
            skLineSegment(sketch, "E9.4.69.0", {"start": v(24.6, 10.04) * mm, "end": v(25.24, 9.28) * mm});
            skArc(sketch, "E9.7.69.0", {"start": v(24.6, 10.04) * mm, "mid": v(23.63, 9.6) * mm, "end": v(22.74, 9.04) * mm});
            skArc(sketch, "E9.11.69.0", {"start": v(25.37, 5.7) * mm, "mid": v(24.68, 6.67) * mm, "end": v(23.95, 7.61) * mm});
            skArc(sketch, "E9.12.69.0", {"start": v(25.24, 9.28) * mm, "mid": v(24.66, 8.4) * mm, "end": v(23.95, 7.61) * mm});
            skLineSegment(sketch, "E9.4.70.0", {"start": v(22.82, 11.9) * mm, "end": v(23.52, 11.2) * mm});
            skArc(sketch, "E9.7.70.0", {"start": v(22.82, 11.9) * mm, "mid": v(21.89, 11.4) * mm, "end": v(21.05, 10.76) * mm});
            skArc(sketch, "E9.11.70.0", {"start": v(23.94, 7.64) * mm, "mid": v(23.17, 8.55) * mm, "end": v(22.37, 9.43) * mm});
            skArc(sketch, "E9.12.70.0", {"start": v(23.52, 11.2) * mm, "mid": v(23.01, 10.27) * mm, "end": v(22.37, 9.43) * mm});
            skLineSegment(sketch, "E9.4.71.0", {"start": v(20.9, 13.63) * mm, "end": v(21.66, 12.98) * mm});
            skArc(sketch, "E9.7.71.0", {"start": v(20.9, 13.63) * mm, "mid": v(20.02, 13.04) * mm, "end": v(19.23, 12.34) * mm});
            skArc(sketch, "E9.11.71.0", {"start": v(22.35, 9.45) * mm, "mid": v(21.52, 10.3) * mm, "end": v(20.65, 11.12) * mm});
            skArc(sketch, "E9.12.71.0", {"start": v(21.66, 12.98) * mm, "mid": v(21.22, 12.01) * mm, "end": v(20.65, 11.12) * mm});
            skLineSegment(sketch, "E9.4.72.0", {"start": v(18.85, 15.19) * mm, "end": v(19.66, 14.6) * mm});
            skArc(sketch, "E9.7.72.0", {"start": v(18.85, 15.19) * mm, "mid": v(18.02, 14.54) * mm, "end": v(17.29, 13.77) * mm});
            skArc(sketch, "E9.11.72.0", {"start": v(20.63, 11.14) * mm, "mid": v(19.73, 11.93) * mm, "end": v(18.8, 12.67) * mm});
            skArc(sketch, "E9.12.72.0", {"start": v(19.66, 14.6) * mm, "mid": v(19.3, 13.6) * mm, "end": v(18.8, 12.67) * mm});
            skLineSegment(sketch, "E9.4.73.0", {"start": v(16.7, 16.58) * mm, "end": v(17.55, 16.06) * mm});
            skArc(sketch, "E9.7.73.0", {"start": v(16.7, 16.58) * mm, "mid": v(15.91, 15.87) * mm, "end": v(15.24, 15.05) * mm});
            skArc(sketch, "E9.11.73.0", {"start": v(18.78, 12.7) * mm, "mid": v(17.82, 13.4) * mm, "end": v(16.84, 14.07) * mm});
            skArc(sketch, "E9.12.73.0", {"start": v(17.55, 16.06) * mm, "mid": v(17.27, 15.04) * mm, "end": v(16.84, 14.07) * mm});
            skLineSegment(sketch, "E9.4.74.0", {"start": v(14.43, 17.8) * mm, "end": v(15.32, 17.35) * mm});
            skArc(sketch, "E9.7.74.0", {"start": v(14.43, 17.8) * mm, "mid": v(13.7, 17.04) * mm, "end": v(13.1, 16.17) * mm});
            skArc(sketch, "E9.11.74.0", {"start": v(16.81, 14.1) * mm, "mid": v(15.8, 14.72) * mm, "end": v(14.77, 15.32) * mm});
            skArc(sketch, "E9.12.74.0", {"start": v(15.32, 17.35) * mm, "mid": v(15.12, 16.31) * mm, "end": v(14.77, 15.32) * mm});
            skLineSegment(sketch, "E9.4.75.0", {"start": v(12.08, 18.85) * mm, "end": v(13, 18.47) * mm});
            skArc(sketch, "E9.7.75.0", {"start": v(12.08, 18.85) * mm, "mid": v(11.42, 18.02) * mm, "end": v(10.88, 17.1) * mm});
            skArc(sketch, "E9.11.75.0", {"start": v(14.75, 15.33) * mm, "mid": v(13.7, 15.88) * mm, "end": v(12.61, 16.4) * mm});
            skArc(sketch, "E9.12.75.0", {"start": v(13, 18.47) * mm, "mid": v(12.88, 17.41) * mm, "end": v(12.61, 16.4) * mm});
            skLineSegment(sketch, "E9.4.76.0", {"start": v(9.65, 19.7) * mm, "end": v(10.6, 19.4) * mm});
            skArc(sketch, "E9.7.76.0", {"start": v(9.65, 19.7) * mm, "mid": v(9.06, 18.83) * mm, "end": v(8.6, 17.87) * mm});
            skArc(sketch, "E9.11.76.0", {"start": v(12.59, 16.4) * mm, "mid": v(11.5, 16.87) * mm, "end": v(10.38, 17.3) * mm});
            skArc(sketch, "E9.12.76.0", {"start": v(10.6, 19.4) * mm, "mid": v(10.57, 18.34) * mm, "end": v(10.38, 17.3) * mm});
            skLineSegment(sketch, "E9.4.77.0", {"start": v(7.16, 20.36) * mm, "end": v(8.14, 20.13) * mm});
            skArc(sketch, "E9.7.77.0", {"start": v(7.16, 20.36) * mm, "mid": v(6.64, 19.44) * mm, "end": v(6.26, 18.46) * mm});
            skArc(sketch, "E9.11.77.0", {"start": v(10.35, 17.3) * mm, "mid": v(9.22, 17.68) * mm, "end": v(8.08, 18.02) * mm});
            skArc(sketch, "E9.12.77.0", {"start": v(8.14, 20.13) * mm, "mid": v(8.18, 19.07) * mm, "end": v(8.08, 18.02) * mm});
            skLineSegment(sketch, "E9.4.78.0", {"start": v(4.63, 20.83) * mm, "end": v(5.62, 20.67) * mm});
            skArc(sketch, "E9.7.78.0", {"start": v(4.63, 20.83) * mm, "mid": v(4.18, 19.87) * mm, "end": v(3.88, 18.86) * mm});
            skArc(sketch, "E9.11.78.0", {"start": v(8.05, 18.03) * mm, "mid": v(6.9, 18.32) * mm, "end": v(5.73, 18.56) * mm});
            skArc(sketch, "E9.12.78.0", {"start": v(5.62, 20.67) * mm, "mid": v(5.75, 19.62) * mm, "end": v(5.73, 18.56) * mm});
            skLineSegment(sketch, "E9.4.79.0", {"start": v(2.07, 21.09) * mm, "end": v(3.07, 21.01) * mm});
            skArc(sketch, "E9.7.79.0", {"start": v(2.07, 21.09) * mm, "mid": v(1.7, 20.1) * mm, "end": v(1.48, 19.07) * mm});
            skArc(sketch, "E9.11.79.0", {"start": v(5.7, 18.57) * mm, "mid": v(4.52, 18.77) * mm, "end": v(3.34, 18.92) * mm});
            skArc(sketch, "E9.12.79.0", {"start": v(3.07, 21.01) * mm, "mid": v(3.28, 19.97) * mm, "end": v(3.34, 18.92) * mm});
            skSolve(sketch);
        }
        {
            var Q0;
            Q0 = qSketchRegion(id + "F0", true);
            extrude(context, id + "F1", {"entities" : qUnion([Q0]), "depth" : 6.35 * mm});
        }
    });
